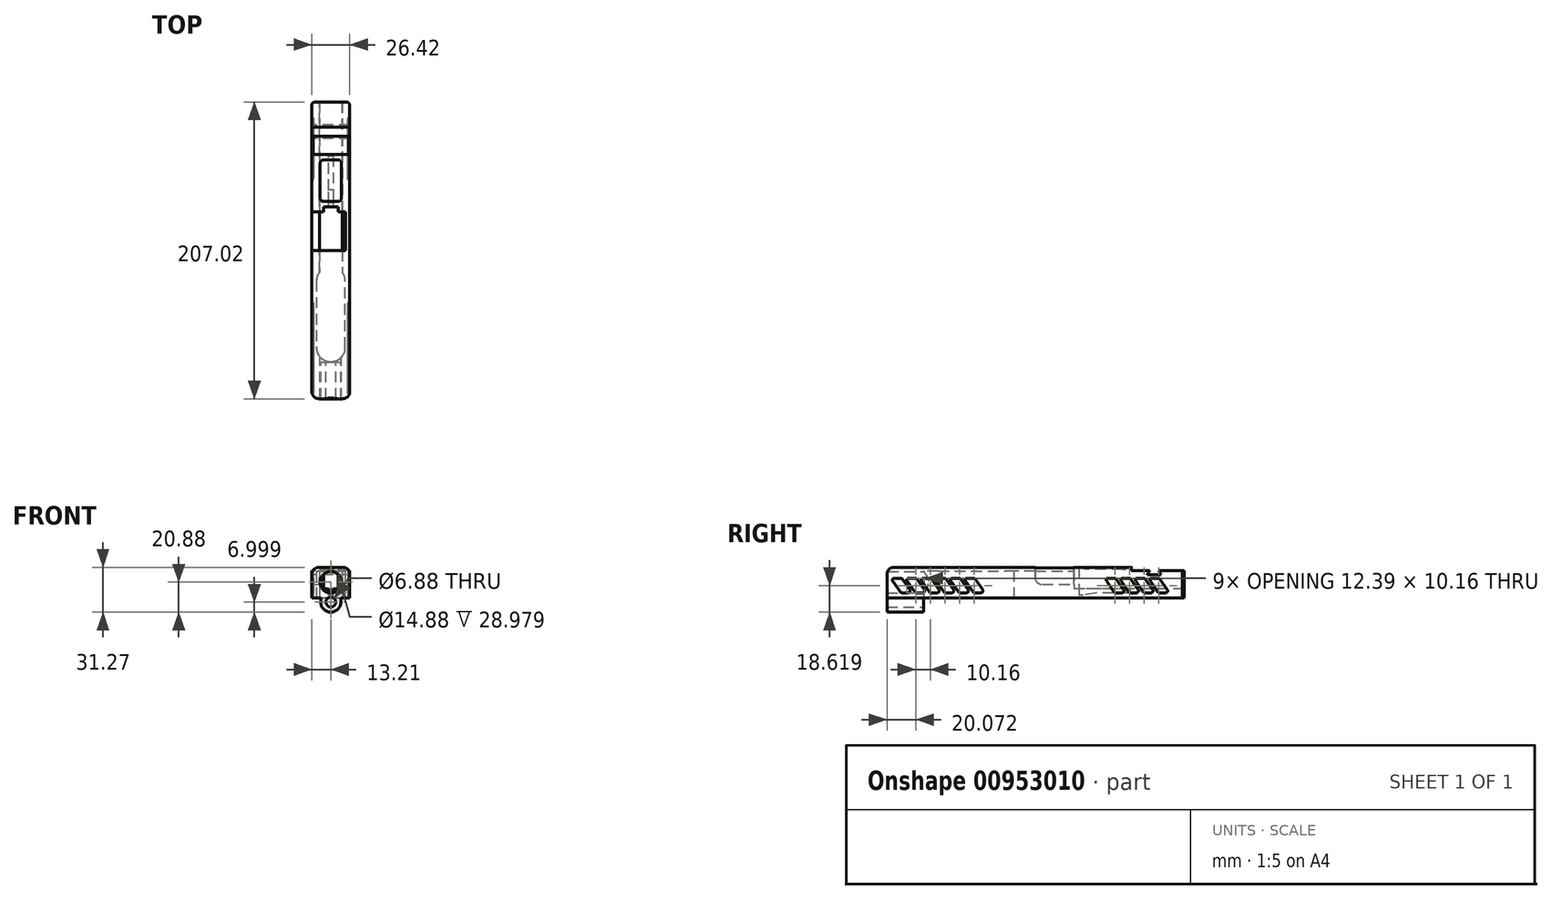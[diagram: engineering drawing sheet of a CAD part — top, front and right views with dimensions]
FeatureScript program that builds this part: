
annotation { "Feature Type Name" : "Feature", "Feature Type Description" : "" }
export const myFeature = defineFeature(function(context is Context, id is Id, definition is map)
    precondition{}
    {
        {
            var Q0;
            Q0=qCreatedBy(makeId("Front.planeOp"),FACE);
            var sketch = newSketch(context, id + "F0", { "sketchPlane" : qUnion([Q0])});
            skLineSegment(sketch, "E0.top", {"start": v(-13.2, 10.39) * mm, "end": v(13.2, 10.39) * mm});
            skLineSegment(sketch, "E0.left", {"start": v(-13.2, -11.1) * mm, "end": v(-13.2, 10.39) * mm});
            skLineSegment(sketch, "E0.right", {"start": v(13.2, -11.1) * mm, "end": v(13.2, 10.39) * mm});
            skLineSegment(sketch, "E1", {"start": v(-13.2, -11.1) * mm, "end": v(-7, -11.1) * mm});
            skLineSegment(sketch, "E2", {"start": v(-7, -11.1) * mm, "end": v(-7, -13.88) * mm});
            skLineSegment(sketch, "E3", {"start": v(13.2, -11.1) * mm, "end": v(7, -11.1) * mm});
            skLineSegment(sketch, "E4", {"start": v(7, -11.1) * mm, "end": v(7, -13.88) * mm});
            skArc(sketch, "E5", {"start": v(-7, -13.88) * mm, "mid": v(0, -20.88) * mm, "end": v(7, -13.88) * mm});
            skCircle(sketch, "E6", {"center": v(0, -13.88) * mm, "radius": 3.44 * mm});
            skCircle(sketch, "E7", {"center": v(0, 0) * mm, "radius": 7.44 * mm});
            skSolve(sketch);
        }
        {
            var Q0;
            Q0=makeQuery(id+"F0.imprint","IMPRINT",FACE,{"disambiguationData":[TD([[makeQuery(id+"F0.imprint","IMPRINT",EDGE,{"derivedFrom":sQuery(id+"F0.wireOp",EDGE,"E0.top")}),-1.0]])]});
            extrude(context, id + "F1", {"entities" : qUnion([Q0]), "endBound" : BoundingType.SYMMETRIC, "depth" : 207 * mm, "offsetDistance" : 25.4 * mm});
        }
        {
            var Q0;
            Q0=makeQuery(id+"F1.opExtrude","SWEPT_FACE",FACE,{"disambiguationData":[OSD([sQuery(id+"F0.wireOp",EDGE,"E0.left")])]});
            var sketch = newSketch(context, id + "F2", { "sketchPlane" : qUnion([Q0])});
            skLineSegment(sketch, "E8.bottom", {"start": v(-103.5, 10.39) * mm, "end": v(103.5, 10.39) * mm});
            skLineSegment(sketch, "E8.left", {"start": v(-103.5, 10.39) * mm, "end": v(-103.5, -11.1) * mm});
            skLineSegment(sketch, "E9", {"start": v(-103.5, -11.1) * mm, "end": v(77.85, -11.1) * mm});
            skLineSegment(sketch, "E10", {"start": v(77.85, -11.1) * mm, "end": v(77.85, -20.93) * mm});
            skLineSegment(sketch, "E11", {"start": v(77.85, -20.93) * mm, "end": v(103.5, -20.93) * mm});
            skLineSegment(sketch, "E12", {"start": v(103.5, -20.93) * mm, "end": v(103.5, 10.39) * mm});
            skSolve(sketch);
        }
        {
            var Q0;
            {var subQ2=sQuery(id+"F2.wireOp",EDGE,"E8.bottom");Q0=makeQuery(id+"F2.imprint","IMPRINT",FACE,{"disambiguationData":[TD([[makeQuery(id+"F2.imprint","IMPRINT",EDGE,{"derivedFrom":subQ2}),1.0]])]});}
            var Q1;
            {var subQ0=sQuery(id+"F2.wireOp",EDGE,"E10");Q1=makeQuery(id+"F2.imprint","IMPRINT",FACE,{"disambiguationData":[TD([[makeQuery(id+"F2.imprint","IMPRINT",EDGE,{"derivedFrom":subQ0}),1.0]])]});}
            extrude(context, id + "F3", {"entities" : qUnion([Q0, Q1]), "operationType" : NewBodyOperationType.INTERSECT, "endBound" : BoundingType.SYMMETRIC, "depth" : 115.82 * mm, "offsetDistance" : 25.4 * mm});
        }
        {
            var Q0;
            Q0=makeQuery(id+"F1.opExtrude","SWEPT_FACE",FACE,{"disambiguationData":[OSD([sQuery(id+"F0.wireOp",EDGE,"E0.top")])]});
            var sketch = newSketch(context, id + "F4", { "sketchPlane" : qUnion([Q0])});
            skLineSegment(sketch, "E13", {"start": v(-8.89, -103.5) * mm, "end": v(-8.89, -61.6) * mm});
            skLineSegment(sketch, "E14", {"start": v(-8.89, -103.5) * mm, "end": v(8.89, -103.5) * mm});
            skLineSegment(sketch, "E15", {"start": v(8.9, -103.5) * mm, "end": v(8.9, -61.6) * mm});
            skArc(sketch, "E16", {"start": v(8.9, -61.6) * mm, "mid": v(0, -52.7) * mm, "end": v(-8.89, -61.6) * mm});
            skLineSegment(sketch, "E17", {"start": v(-8.89, -61.6) * mm, "end": v(-8.9, -33.66) * mm});
            skLineSegment(sketch, "E18", {"start": v(-8.89, -33.66) * mm, "end": v(8.89, -33.66) * mm});
            skLineSegment(sketch, "E19", {"start": v(8.89, -33.66) * mm, "end": v(8.9, -61.6) * mm});
            skSolve(sketch);
        }
        {
            var Q0;
            Q0=makeQuery(id+"F1.opExtrude","SWEPT_FACE",FACE,{"disambiguationData":[OSD([sQuery(id+"F0.wireOp",EDGE,"E0.left")])]});
            var sketch = newSketch(context, id + "F5", { "sketchPlane" : qUnion([Q0])});
            skLineSegment(sketch, "E20", {"start": v(-93.35, -7.34) * mm, "end": v(-86.23, 2.82) * mm});
            skLineSegment(sketch, "E21", {"start": v(-86.23, 2.82) * mm, "end": v(-78.61, 2.82) * mm});
            skLineSegment(sketch, "E22", {"start": v(-78.61, 2.82) * mm, "end": v(-85.73, -7.34) * mm});
            skLineSegment(sketch, "E23", {"start": v(-85.73, -7.34) * mm, "end": v(-93.35, -7.34) * mm});
            skLineSegment(sketch, "E24", {"start": v(-83.19, -7.34) * mm, "end": v(-76.07, 2.82) * mm});
            skLineSegment(sketch, "E25", {"start": v(-76.07, 2.82) * mm, "end": v(-68.45, 2.82) * mm});
            skLineSegment(sketch, "E26", {"start": v(-68.45, 2.82) * mm, "end": v(-75.57, -7.34) * mm});
            skLineSegment(sketch, "E27", {"start": v(-75.57, -7.34) * mm, "end": v(-83.19, -7.34) * mm});
            skLineSegment(sketch, "E28", {"start": v(-73.03, -7.34) * mm, "end": v(-65.91, 2.82) * mm});
            skLineSegment(sketch, "E29", {"start": v(-65.91, 2.82) * mm, "end": v(-58.3, 2.82) * mm});
            skLineSegment(sketch, "E30", {"start": v(-58.3, 2.82) * mm, "end": v(-65.4, -7.34) * mm});
            skLineSegment(sketch, "E31", {"start": v(-65.4, -7.34) * mm, "end": v(-73.03, -7.34) * mm});
            skLineSegment(sketch, "E32", {"start": v(-62.87, -7.34) * mm, "end": v(-55.75, 2.82) * mm});
            skLineSegment(sketch, "E33", {"start": v(-55.75, 2.82) * mm, "end": v(-48.13, 2.82) * mm});
            skLineSegment(sketch, "E34", {"start": v(-48.13, 2.82) * mm, "end": v(-55.25, -7.34) * mm});
            skLineSegment(sketch, "E35", {"start": v(-55.25, -7.34) * mm, "end": v(-62.87, -7.34) * mm});
            skLineSegment(sketch, "E36", {"start": v(45.6, -7.34) * mm, "end": v(52.7, 2.82) * mm});
            skLineSegment(sketch, "E37", {"start": v(52.7, 2.82) * mm, "end": v(60.33, 2.82) * mm});
            skLineSegment(sketch, "E38", {"start": v(60.33, 2.82) * mm, "end": v(53.21, -7.34) * mm});
            skLineSegment(sketch, "E39", {"start": v(53.21, -7.34) * mm, "end": v(45.6, -7.34) * mm});
            skLineSegment(sketch, "E40", {"start": v(55.75, -7.34) * mm, "end": v(62.87, 2.82) * mm});
            skLineSegment(sketch, "E41", {"start": v(62.87, 2.82) * mm, "end": v(70.49, 2.82) * mm});
            skLineSegment(sketch, "E42", {"start": v(70.49, 2.82) * mm, "end": v(63.37, -7.34) * mm});
            skLineSegment(sketch, "E43", {"start": v(63.37, -7.34) * mm, "end": v(55.75, -7.34) * mm});
            skLineSegment(sketch, "E44", {"start": v(65.91, -7.34) * mm, "end": v(73.03, 2.82) * mm});
            skLineSegment(sketch, "E45", {"start": v(73.03, 2.82) * mm, "end": v(80.65, 2.82) * mm});
            skLineSegment(sketch, "E46", {"start": v(80.65, 2.82) * mm, "end": v(73.53, -7.34) * mm});
            skLineSegment(sketch, "E47", {"start": v(73.53, -7.34) * mm, "end": v(65.91, -7.34) * mm});
            skLineSegment(sketch, "E48", {"start": v(76.07, -7.34) * mm, "end": v(83.19, 2.82) * mm});
            skLineSegment(sketch, "E49", {"start": v(83.19, 2.82) * mm, "end": v(90.8, 2.82) * mm});
            skLineSegment(sketch, "E50", {"start": v(90.8, 2.82) * mm, "end": v(83.7, -7.34) * mm});
            skLineSegment(sketch, "E51", {"start": v(83.7, -7.34) * mm, "end": v(76.07, -7.34) * mm});
            skLineSegment(sketch, "E52", {"start": v(35.43, -7.34) * mm, "end": v(42.55, 2.82) * mm});
            skLineSegment(sketch, "E53", {"start": v(42.55, 2.82) * mm, "end": v(50.17, 2.82) * mm});
            skLineSegment(sketch, "E54", {"start": v(50.17, 2.82) * mm, "end": v(43.05, -7.34) * mm});
            skLineSegment(sketch, "E55", {"start": v(43.05, -7.34) * mm, "end": v(35.43, -7.34) * mm});
            skLineSegment(sketch, "E56", {"start": v(86.23, -7.34) * mm, "end": v(93.35, 2.82) * mm});
            skLineSegment(sketch, "E57", {"start": v(93.35, 2.82) * mm, "end": v(100.97, 2.82) * mm});
            skLineSegment(sketch, "E58", {"start": v(100.97, 2.82) * mm, "end": v(93.85, -7.34) * mm});
            skLineSegment(sketch, "E59", {"start": v(93.85, -7.34) * mm, "end": v(86.23, -7.34) * mm});
            skSolve(sketch);
        }
        {
            var Q0;
            Q0=makeQuery(id+"F3.boolean.opBoolean","MERGE",FACE,{"derivedFrom":[makeQuery(id+"F1.opExtrude","SWEPT_FACE",FACE,{"disambiguationData":[OSD([sQuery(id+"F0.wireOp",EDGE,"E3")])]})],"fromTools":[makeQuery(id+"F3.boolean.toolComplement.opBoolean","COPY",FACE,{"derivedFrom":makeQuery(id+"F3.opExtrude","SWEPT_FACE",FACE,{"disambiguationData":[OSD([sQuery(id+"F2.wireOp",EDGE,"E9")])]})})]});
            var sketch = newSketch(context, id + "F6", { "sketchPlane" : qUnion([Q0])});
            skLineSegment(sketch, "E60.left", {"start": v(-10, 21.26) * mm, "end": v(-10, 67.84) * mm});
            skLineSegment(sketch, "E61", {"start": v(-8, -26.72) * mm, "end": v(-5, -26.72) * mm});
            skLineSegment(sketch, "E62", {"start": v(-5, -26.72) * mm, "end": v(-5, -30.22) * mm});
            skLineSegment(sketch, "E63", {"start": v(-5, -30.22) * mm, "end": v(5, -30.22) * mm});
            skLineSegment(sketch, "E64", {"start": v(5, -30.22) * mm, "end": v(5, -26.72) * mm});
            skLineSegment(sketch, "E65", {"start": v(5, -26.72) * mm, "end": v(8, -26.72) * mm});
            skArc(sketch, "E66", {"start": v(-10, 21.26) * mm, "mid": v(-9.5, 18.1) * mm, "end": v(-8, 15.25) * mm});
            skArc(sketch, "E67", {"start": v(10, 67.84) * mm, "mid": v(0, 77.85) * mm, "end": v(-10, 67.84) * mm});
            skLineSegment(sketch, "E68", {"start": v(10, 67.84) * mm, "end": v(10, 21.26) * mm});
            skArc(sketch, "E69", {"start": v(8, 15.25) * mm, "mid": v(9.5, 18.1) * mm, "end": v(10, 21.26) * mm});
            skLineSegment(sketch, "E70", {"start": v(-8, 0.28) * mm, "end": v(-8, 15.25) * mm});
            skLineSegment(sketch, "E71", {"start": v(-8, 0.28) * mm, "end": v(8, 0.28) * mm});
            skLineSegment(sketch, "E72", {"start": v(-8, 0.28) * mm, "end": v(-8, -26.72) * mm});
            skLineSegment(sketch, "E73", {"start": v(8, -26.72) * mm, "end": v(8, 0.28) * mm});
            skLineSegment(sketch, "E74", {"start": v(8, 0.28) * mm, "end": v(8, 15.25) * mm});
            skLineSegment(sketch, "E75", {"start": v(8, -26.72) * mm, "end": v(8, -103.5) * mm});
            skLineSegment(sketch, "E76", {"start": v(8, -103.5) * mm, "end": v(-8, -103.5) * mm});
            skLineSegment(sketch, "E77", {"start": v(-8, -103.5) * mm, "end": v(-8, -26.72) * mm});
            skLineSegment(sketch, "E78", {"start": v(-1.5, -30.22) * mm, "end": v(-1.5, -65.73) * mm});
            skLineSegment(sketch, "E79", {"start": v(-1.5, -65.73) * mm, "end": v(1.5, -65.73) * mm});
            skLineSegment(sketch, "E80", {"start": v(1.5, -65.73) * mm, "end": v(1.5, -30.22) * mm});
            skLineSegment(sketch, "E81", {"start": v(-1.5, -33.22) * mm, "end": v(1.5, -33.22) * mm});
            skLineSegment(sketch, "E82", {"start": v(-1.5, -42.21) * mm, "end": v(1.5, -42.21) * mm});
            skSolve(sketch);
        }
        {
            var Q0;
            Q0=makeQuery(id+"F6.imprint","IMPRINT",FACE,{"disambiguationData":[TD([[makeQuery(id+"F6.imprint","IMPRINT",EDGE,{"derivedFrom":sQuery(id+"F6.wireOp",EDGE,"E61")}),1.0]])]});
            var Q1;
            {var subQ0=sQuery(id+"F6.wireOp",EDGE,"E64");Q1=makeQuery(id+"F6.imprint","IMPRINT",FACE,{"disambiguationData":[TD([[makeQuery(id+"F6.imprint","IMPRINT",EDGE,{"derivedFrom":subQ0}),1.0]])]});}
            extrude(context, id + "F7", {"entities" : qUnion([Q0, Q1]), "operationType" : NewBodyOperationType.REMOVE, "oppositeDirection" : true, "depth" : 25.4 * mm, "offsetDistance" : 25.4 * mm});
        }
        {
            var Q0;
            {var subQ1=sQuery(id+"F6.wireOp",EDGE,"E60.left");Q0=makeQuery(id+"F6.imprint","IMPRINT",FACE,{"disambiguationData":[TD([[makeQuery(id+"F6.imprint","IMPRINT",EDGE,{"derivedFrom":subQ1}),-1.0]])]});}
            var Q1;
            {var subQ6=sQuery(id+"F6.wireOp",EDGE,"E68");Q1=makeQuery(id+"F6.imprint","IMPRINT",FACE,{"disambiguationData":[TD([[makeQuery(id+"F6.imprint","IMPRINT",EDGE,{"derivedFrom":subQ6}),-1.0]])]});}
            extrude(context, id + "F8", {"entities" : qUnion([Q0, Q1]), "operationType" : NewBodyOperationType.REMOVE, "oppositeDirection" : true, "depth" : 19 * mm, "offsetDistance" : 25.4 * mm});
        }
        {
            var Q0;
            Q0=makeQuery(id+"F8.boolean.opBoolean","MERGE",FACE,{"derivedFrom":[makeQuery(id+"F7.boolean.opBoolean","COPY",FACE,{"derivedFrom":makeQuery(id+"F7.opExtrude","SWEPT_FACE",FACE,{"disambiguationData":[OSD([sQuery(id+"F6.wireOp",EDGE,"E72")])]})})],"fromTools":[makeQuery(id+"F8.opExtrude","SWEPT_FACE",FACE,{"disambiguationData":[OSD([sQuery(id+"F6.wireOp",EDGE,"E70")])]})]});
            var sketch = newSketch(context, id + "F9", { "sketchPlane" : qUnion([Q0])});
            skLineSegment(sketch, "E83.bottom", {"start": v(-0.28, 10.39) * mm, "end": v(26.72, 10.39) * mm});
            skLineSegment(sketch, "E83.top", {"start": v(-0.28, -1.6) * mm, "end": v(26.72, -1.6) * mm});
            skLineSegment(sketch, "E83.left", {"start": v(-0.28, 10.39) * mm, "end": v(-0.28, -1.6) * mm});
            skLineSegment(sketch, "E83.right", {"start": v(26.72, 10.39) * mm, "end": v(26.72, -1.6) * mm});
            skSolve(sketch);
        }
        {
            var Q0;
            Q0=makeQuery(id+"F7.boolean.opBoolean","INTERSECT",EDGE,{"derivedFrom":[makeQuery(id+"F1.opExtrude","SWEPT_FACE",FACE,{"disambiguationData":[OSD([sQuery(id+"F0.wireOp",EDGE,"E0.top")])]}),makeQuery(id+"F7.opExtrude","SWEPT_FACE",FACE,{"disambiguationData":[OSD([sQuery(id+"F6.wireOp",EDGE,"E73")])]})]});
            chamfer(context, id + "F10", {"entities" : qUnion([Q0]), "width" : 2.5 * mm, "tangentPropagation" : true});
        }
        {
            var Q0;
            {var subQ5=sQuery(id+"F6.wireOp",EDGE,"E81");Q0=makeQuery(id+"F6.imprint","IMPRINT",FACE,{"disambiguationData":[TD([[makeQuery(id+"F6.imprint","IMPRINT",EDGE,{"derivedFrom":subQ5}),1.0]])]});}
            var Q1;
            {var subQ0=sQuery(id+"F6.wireOp",EDGE,"E81");Q1=makeQuery(id+"F6.imprint","IMPRINT",FACE,{"disambiguationData":[TD([[makeQuery(id+"F6.imprint","IMPRINT",EDGE,{"derivedFrom":subQ0}),-1.0]])]});}
            var Q2;
            {var subQ0=sQuery(id+"F6.wireOp",EDGE,"E79");Q2=makeQuery(id+"F6.imprint","IMPRINT",FACE,{"disambiguationData":[TD([[makeQuery(id+"F6.imprint","IMPRINT",EDGE,{"derivedFrom":subQ0}),1.0]])]});}
            var Q3;
            Q3=makeQuery(id+"F6.imprint","IMPRINT",FACE,{"disambiguationData":[TD([[makeQuery(id+"F6.imprint","IMPRINT",EDGE,{"derivedFrom":sQuery(id+"F6.wireOp",EDGE,"E61")}),-1.0]])]});
            var Q4;
            {var subQ1=sQuery(id+"F6.wireOp",EDGE,"E64");Q4=makeQuery(id+"F6.imprint","IMPRINT",FACE,{"disambiguationData":[TD([[makeQuery(id+"F6.imprint","IMPRINT",EDGE,{"derivedFrom":subQ1}),-1.0]])]});}
            var Q5;
            Q5=makeQuery(id+"F10.opChamfer","SPLIT",FACE,{"disambiguationData":[OD(1.0)],"derivedFrom":makeQuery(id+"F1.opExtrude","SWEPT_FACE",FACE,{"disambiguationData":[OSD([sQuery(id+"F0.wireOp",EDGE,"E0.top")])]})});
            extrude(context, id + "F11", {"entities" : qUnion([Q0, Q1, Q2, Q3, Q4]), "operationType" : NewBodyOperationType.ADD, "endBound" : BoundingType.UP_TO_SURFACE, "oppositeDirection" : true, "depth" : 25.4 * mm, "endBoundEntityFace" : qUnion([Q5]), "offsetDistance" : 25.4 * mm});
        }
        {
            var Q0;
            Q0=makeQuery(id+"F6.imprint","IMPRINT",FACE,{"disambiguationData":[TD([[makeQuery(id+"F6.imprint","IMPRINT",EDGE,{"derivedFrom":sQuery(id+"F6.wireOp",EDGE,"E61")}),-1.0]])]});
            var Q1;
            {var subQ1=sQuery(id+"F6.wireOp",EDGE,"E64");Q1=makeQuery(id+"F6.imprint","IMPRINT",FACE,{"disambiguationData":[TD([[makeQuery(id+"F6.imprint","IMPRINT",EDGE,{"derivedFrom":subQ1}),-1.0]])]});}
            extrude(context, id + "F12", {"entities" : qUnion([Q0, Q1]), "operationType" : NewBodyOperationType.REMOVE, "oppositeDirection" : true, "depth" : 6.48 * mm, "offsetDistance" : 25.4 * mm});
        }
        {
            var Q0;
            {var subQ5=sQuery(id+"F6.wireOp",EDGE,"E81");Q0=makeQuery(id+"F6.imprint","IMPRINT",FACE,{"disambiguationData":[TD([[makeQuery(id+"F6.imprint","IMPRINT",EDGE,{"derivedFrom":subQ5}),1.0]])]});}
            extrude(context, id + "F13", {"entities" : qUnion([Q0]), "operationType" : NewBodyOperationType.ADD, "oppositeDirection" : true, "depth" : 1.98 * mm, "offsetDistance" : 25.4 * mm});
        }
        {
            var Q0;
            Q0=makeQuery(id+"F12.boolean.opBoolean","COPY",FACE,{"derivedFrom":makeQuery(id+"F12.opExtrude","SWEPT_FACE",FACE,{"disambiguationData":[OSD([sQuery(id+"F6.wireOp",EDGE,"E78")])]})});
            var sketch = newSketch(context, id + "F14", { "sketchPlane" : qUnion([Q0])});
            skLineSegment(sketch, "E84", {"start": v(-30.22, -11.1) * mm, "end": v(-30.22, -9.12) * mm});
            skLineSegment(sketch, "E85", {"start": v(-30.22, -9.12) * mm, "end": v(-33.22, -9.12) * mm});
            skLineSegment(sketch, "E86", {"start": v(-33.22, -9.12) * mm, "end": v(-42.21, -7.62) * mm});
            skLineSegment(sketch, "E87", {"start": v(-42.21, -7.62) * mm, "end": v(-65.73, -7.62) * mm});
            skPoint(sketch, "E87.endSnap0", {"position": v(-65.73, -7.86) * mm});
            skLineSegment(sketch, "E88", {"start": v(-65.73, -7.62) * mm, "end": v(-65.73, -11.1) * mm});
            skLineSegment(sketch, "E89", {"start": v(-65.73, -11.1) * mm, "end": v(-30.22, -11.1) * mm});
            skSolve(sketch);
        }
        {
            var Q0;
            Q0=makeQuery(id+"F14.imprint","IMPRINT",FACE,{"disambiguationData":[TD([[makeQuery(id+"F14.imprint","IMPRINT",EDGE,{"derivedFrom":sQuery(id+"F14.wireOp",EDGE,"E84")}),-1.0]])]});
            extrude(context, id + "F15", {"entities" : qUnion([Q0]), "operationType" : NewBodyOperationType.REMOVE, "oppositeDirection" : true, "depth" : 4.06 * mm, "offsetDistance" : 25.4 * mm});
        }
        {
            var Q0;
            Q0=makeQuery(id+"F1.opExtrude","SWEPT_FACE",FACE,{"disambiguationData":[OSD([sQuery(id+"F0.wireOp",EDGE,"E0.left")])]});
            var sketch = newSketch(context, id + "F16", { "sketchPlane" : qUnion([Q0])});
            skLineSegment(sketch, "E90", {"start": v(-103.5, 11.76) * mm, "end": v(-66.93, 11.76) * mm});
            skLineSegment(sketch, "E91", {"start": v(-66.93, 11.76) * mm, "end": v(-66.93, 7.95) * mm});
            skLineSegment(sketch, "E92", {"start": v(-66.93, 7.95) * mm, "end": v(-79.44, 7.95) * mm});
            skLineSegment(sketch, "E93", {"start": v(-79.44, 7.95) * mm, "end": v(-77.9, 5.28) * mm});
            skLineSegment(sketch, "E94", {"start": v(-77.9, 5.28) * mm, "end": v(-87.43, 5.28) * mm});
            skLineSegment(sketch, "E95", {"start": v(-87.43, 5.28) * mm, "end": v(-85.89, 7.95) * mm});
            skLineSegment(sketch, "E96", {"start": v(-85.89, 7.95) * mm, "end": v(-103.5, 7.95) * mm});
            skLineSegment(sketch, "E97", {"start": v(-103.5, 11.76) * mm, "end": v(-103.5, 7.95) * mm});
            skSolve(sketch);
        }
        {
            var Q0;
            {var subQ9=sQuery(id+"F16.wireOp",EDGE,"E90");Q0=makeQuery(id+"F16.imprint","IMPRINT",FACE,{"disambiguationData":[TD([[makeQuery(id+"F16.imprint","IMPRINT",EDGE,{"derivedFrom":subQ9}),-1.0]])]});}
            var Q1;
            {var subQ8=sQuery(id+"F16.wireOp",EDGE,"IXoennea-lvBA-JRsV-betp-ysQFHRv7K1wK");Q1=makeQuery(id+"F16.imprint","IMPRINT",FACE,{"disambiguationData":[TD([[makeQuery(id+"F16.imprint","IMPRINT",EDGE,{"derivedFrom":subQ8}),1.0]])]});}
            var Q2;
            {var subQ0=sQuery(id+"F16.wireOp",EDGE,"E93");Q2=makeQuery(id+"F16.imprint","IMPRINT",FACE,{"disambiguationData":[TD([[makeQuery(id+"F16.imprint","IMPRINT",EDGE,{"derivedFrom":subQ0}),-1.0]])]});}
            extrude(context, id + "F17", {"entities" : qUnion([Q0, Q1, Q2]), "operationType" : NewBodyOperationType.REMOVE, "oppositeDirection" : true, "depth" : 44.2 * mm, "offsetDistance" : 25.4 * mm});
        }
        {
            var Q0;
            Q0=makeQuery(id+"F5.imprint","IMPRINT",FACE,{"disambiguationData":[TD([[makeQuery(id+"F5.imprint","IMPRINT",EDGE,{"derivedFrom":sQuery(id+"F5.wireOp",EDGE,"E20")}),-1.0]])]});
            var Q1;
            Q1=makeQuery(id+"F5.imprint","IMPRINT",FACE,{"disambiguationData":[TD([[makeQuery(id+"F5.imprint","IMPRINT",EDGE,{"derivedFrom":sQuery(id+"F5.wireOp",EDGE,"E24")}),-1.0]])]});
            var Q2;
            Q2=makeQuery(id+"F5.imprint","IMPRINT",FACE,{"disambiguationData":[TD([[makeQuery(id+"F5.imprint","IMPRINT",EDGE,{"derivedFrom":sQuery(id+"F5.wireOp",EDGE,"E28")}),-1.0]])]});
            var Q3;
            Q3=makeQuery(id+"F5.imprint","IMPRINT",FACE,{"disambiguationData":[TD([[makeQuery(id+"F5.imprint","IMPRINT",EDGE,{"derivedFrom":sQuery(id+"F5.wireOp",EDGE,"E32")}),-1.0]])]});
            var Q4;
            Q4=qSketchRegion(id+"F9",true);
            var Q5;
            Q5=makeQuery(id+"F5.imprint","IMPRINT",FACE,{"disambiguationData":[TD([[makeQuery(id+"F5.imprint","IMPRINT",EDGE,{"derivedFrom":sQuery(id+"F5.wireOp",EDGE,"E36")}),-1.0]])]});
            var Q6;
            Q6=makeQuery(id+"F5.imprint","IMPRINT",FACE,{"disambiguationData":[TD([[makeQuery(id+"F5.imprint","IMPRINT",EDGE,{"derivedFrom":sQuery(id+"F5.wireOp",EDGE,"E40")}),-1.0]])]});
            var Q7;
            Q7=makeQuery(id+"F5.imprint","IMPRINT",FACE,{"disambiguationData":[TD([[makeQuery(id+"F5.imprint","IMPRINT",EDGE,{"derivedFrom":sQuery(id+"F5.wireOp",EDGE,"E44")}),-1.0]])]});
            var Q8;
            Q8=makeQuery(id+"F5.imprint","IMPRINT",FACE,{"disambiguationData":[TD([[makeQuery(id+"F5.imprint","IMPRINT",EDGE,{"derivedFrom":sQuery(id+"F5.wireOp",EDGE,"E48")}),-1.0]])]});
            var Q9;
            Q9=makeQuery(id+"F5.imprint","IMPRINT",FACE,{"disambiguationData":[TD([[makeQuery(id+"F5.imprint","IMPRINT",EDGE,{"derivedFrom":sQuery(id+"F5.wireOp",EDGE,"E52")}),-1.0]])]});
            var Q10;
            Q10=makeQuery(id+"F5.imprint","IMPRINT",FACE,{"disambiguationData":[TD([[makeQuery(id+"F5.imprint","IMPRINT",EDGE,{"derivedFrom":sQuery(id+"F5.wireOp",EDGE,"E56")}),-1.0]])]});
            extrude(context, id + "F18", {"entities" : qUnion([Q0, Q1, Q2, Q3, Q4, Q5, Q6, Q7, Q8, Q9, Q10]), "operationType" : NewBodyOperationType.REMOVE, "oppositeDirection" : true, "depth" : 1.27 * mm, "offsetDistance" : 25.4 * mm});
        }
        {
            var Q0;
            Q0=makeQuery(id+"F18.boolean.opBoolean","COPY",EDGE,{"derivedFrom":makeQuery(id+"F18.opExtrude","SWEPT_EDGE",EDGE,{"disambiguationData":[OSD([sQuery(id+"F5.wireOp",EDGE,"E20"),sQuery(id+"F5.wireOp",EDGE,"E21")])]})});
            var Q1;
            Q1=makeQuery(id+"F18.boolean.opBoolean","COPY",EDGE,{"derivedFrom":makeQuery(id+"F18.opExtrude","SWEPT_EDGE",EDGE,{"disambiguationData":[OSD([sQuery(id+"F5.wireOp",EDGE,"E24"),sQuery(id+"F5.wireOp",EDGE,"E25")])]})});
            var Q2;
            Q2=makeQuery(id+"F18.boolean.opBoolean","COPY",EDGE,{"derivedFrom":makeQuery(id+"F18.opExtrude","SWEPT_EDGE",EDGE,{"disambiguationData":[OSD([sQuery(id+"F5.wireOp",EDGE,"E28"),sQuery(id+"F5.wireOp",EDGE,"E29")])]})});
            var Q3;
            Q3=makeQuery(id+"F18.boolean.opBoolean","COPY",EDGE,{"derivedFrom":makeQuery(id+"F18.opExtrude","SWEPT_EDGE",EDGE,{"disambiguationData":[OSD([sQuery(id+"F5.wireOp",EDGE,"E32"),sQuery(id+"F5.wireOp",EDGE,"E33")])]})});
            var Q4;
            Q4=makeQuery(id+"F18.boolean.opBoolean","COPY",EDGE,{"derivedFrom":makeQuery(id+"F18.opExtrude","SWEPT_EDGE",EDGE,{"disambiguationData":[OSD([sQuery(id+"F5.wireOp",EDGE,"E21"),sQuery(id+"F5.wireOp",EDGE,"E22")])]})});
            var Q5;
            Q5=makeQuery(id+"F18.boolean.opBoolean","COPY",EDGE,{"derivedFrom":makeQuery(id+"F18.opExtrude","SWEPT_EDGE",EDGE,{"disambiguationData":[OSD([sQuery(id+"F5.wireOp",EDGE,"E25"),sQuery(id+"F5.wireOp",EDGE,"E26")])]})});
            var Q6;
            Q6=makeQuery(id+"F18.boolean.opBoolean","COPY",EDGE,{"derivedFrom":makeQuery(id+"F18.opExtrude","SWEPT_EDGE",EDGE,{"disambiguationData":[OSD([sQuery(id+"F5.wireOp",EDGE,"E29"),sQuery(id+"F5.wireOp",EDGE,"E30")])]})});
            var Q7;
            Q7=makeQuery(id+"F18.boolean.opBoolean","COPY",EDGE,{"derivedFrom":makeQuery(id+"F18.opExtrude","SWEPT_EDGE",EDGE,{"disambiguationData":[OSD([sQuery(id+"F5.wireOp",EDGE,"E33"),sQuery(id+"F5.wireOp",EDGE,"E34")])]})});
            var Q8;
            Q8=makeQuery(id+"F18.boolean.opBoolean","COPY",EDGE,{"derivedFrom":makeQuery(id+"F18.opExtrude","SWEPT_EDGE",EDGE,{"disambiguationData":[OSD([sQuery(id+"F5.wireOp",EDGE,"E34"),sQuery(id+"F5.wireOp",EDGE,"E35")])]})});
            var Q9;
            Q9=makeQuery(id+"F18.boolean.opBoolean","COPY",EDGE,{"derivedFrom":makeQuery(id+"F18.opExtrude","SWEPT_EDGE",EDGE,{"disambiguationData":[OSD([sQuery(id+"F5.wireOp",EDGE,"E30"),sQuery(id+"F5.wireOp",EDGE,"E31")])]})});
            var Q10;
            Q10=makeQuery(id+"F18.boolean.opBoolean","COPY",EDGE,{"derivedFrom":makeQuery(id+"F18.opExtrude","SWEPT_EDGE",EDGE,{"disambiguationData":[OSD([sQuery(id+"F5.wireOp",EDGE,"E26"),sQuery(id+"F5.wireOp",EDGE,"E27")])]})});
            var Q11;
            Q11=makeQuery(id+"F18.boolean.opBoolean","COPY",EDGE,{"derivedFrom":makeQuery(id+"F18.opExtrude","SWEPT_EDGE",EDGE,{"disambiguationData":[OSD([sQuery(id+"F5.wireOp",EDGE,"E22"),sQuery(id+"F5.wireOp",EDGE,"E23")])]})});
            var Q12;
            Q12=makeQuery(id+"F18.boolean.opBoolean","COPY",EDGE,{"derivedFrom":makeQuery(id+"F18.opExtrude","SWEPT_EDGE",EDGE,{"disambiguationData":[OSD([sQuery(id+"F5.wireOp",EDGE,"E20"),sQuery(id+"F5.wireOp",EDGE,"E23")])]})});
            var Q13;
            Q13=makeQuery(id+"F18.boolean.opBoolean","COPY",EDGE,{"derivedFrom":makeQuery(id+"F18.opExtrude","SWEPT_EDGE",EDGE,{"disambiguationData":[OSD([sQuery(id+"F5.wireOp",EDGE,"E24"),sQuery(id+"F5.wireOp",EDGE,"E27")])]})});
            var Q14;
            Q14=makeQuery(id+"F18.boolean.opBoolean","COPY",EDGE,{"derivedFrom":makeQuery(id+"F18.opExtrude","SWEPT_EDGE",EDGE,{"disambiguationData":[OSD([sQuery(id+"F5.wireOp",EDGE,"E28"),sQuery(id+"F5.wireOp",EDGE,"E31")])]})});
            var Q15;
            Q15=makeQuery(id+"F18.boolean.opBoolean","COPY",EDGE,{"derivedFrom":makeQuery(id+"F18.opExtrude","SWEPT_EDGE",EDGE,{"disambiguationData":[OSD([sQuery(id+"F5.wireOp",EDGE,"E32"),sQuery(id+"F5.wireOp",EDGE,"E35")])]})});
            var Q16;
            Q16=makeQuery(id+"F18.boolean.opBoolean","COPY",EDGE,{"derivedFrom":makeQuery(id+"F18.opExtrude","SWEPT_EDGE",EDGE,{"disambiguationData":[OSD([sQuery(id+"F5.wireOp",EDGE,"E37"),sQuery(id+"F5.wireOp",EDGE,"E38")])]})});
            var Q17;
            Q17=makeQuery(id+"F18.boolean.opBoolean","COPY",EDGE,{"derivedFrom":makeQuery(id+"F18.opExtrude","SWEPT_EDGE",EDGE,{"disambiguationData":[OSD([sQuery(id+"F5.wireOp",EDGE,"E41"),sQuery(id+"F5.wireOp",EDGE,"E42")])]})});
            var Q18;
            Q18=makeQuery(id+"F18.boolean.opBoolean","COPY",EDGE,{"derivedFrom":makeQuery(id+"F18.opExtrude","SWEPT_EDGE",EDGE,{"disambiguationData":[OSD([sQuery(id+"F5.wireOp",EDGE,"E45"),sQuery(id+"F5.wireOp",EDGE,"E46")])]})});
            var Q19;
            Q19=makeQuery(id+"F18.boolean.opBoolean","COPY",EDGE,{"derivedFrom":makeQuery(id+"F18.opExtrude","SWEPT_EDGE",EDGE,{"disambiguationData":[OSD([sQuery(id+"F5.wireOp",EDGE,"E49"),sQuery(id+"F5.wireOp",EDGE,"E50")])]})});
            var Q20;
            Q20=makeQuery(id+"F18.boolean.opBoolean","COPY",EDGE,{"derivedFrom":makeQuery(id+"F18.opExtrude","SWEPT_EDGE",EDGE,{"disambiguationData":[OSD([sQuery(id+"F5.wireOp",EDGE,"E50"),sQuery(id+"F5.wireOp",EDGE,"E51")])]})});
            var Q21;
            Q21=makeQuery(id+"F18.boolean.opBoolean","COPY",EDGE,{"derivedFrom":makeQuery(id+"F18.opExtrude","SWEPT_EDGE",EDGE,{"disambiguationData":[OSD([sQuery(id+"F5.wireOp",EDGE,"E46"),sQuery(id+"F5.wireOp",EDGE,"E47")])]})});
            var Q22;
            Q22=makeQuery(id+"F18.boolean.opBoolean","COPY",EDGE,{"derivedFrom":makeQuery(id+"F18.opExtrude","SWEPT_EDGE",EDGE,{"disambiguationData":[OSD([sQuery(id+"F5.wireOp",EDGE,"E42"),sQuery(id+"F5.wireOp",EDGE,"E43")])]})});
            var Q23;
            Q23=makeQuery(id+"F18.boolean.opBoolean","COPY",EDGE,{"derivedFrom":makeQuery(id+"F18.opExtrude","SWEPT_EDGE",EDGE,{"disambiguationData":[OSD([sQuery(id+"F5.wireOp",EDGE,"E38"),sQuery(id+"F5.wireOp",EDGE,"E39")])]})});
            var Q24;
            Q24=makeQuery(id+"F18.boolean.opBoolean","COPY",EDGE,{"derivedFrom":makeQuery(id+"F18.opExtrude","SWEPT_EDGE",EDGE,{"disambiguationData":[OSD([sQuery(id+"F5.wireOp",EDGE,"E48"),sQuery(id+"F5.wireOp",EDGE,"E51")])]})});
            var Q25;
            Q25=makeQuery(id+"F18.boolean.opBoolean","COPY",EDGE,{"derivedFrom":makeQuery(id+"F18.opExtrude","SWEPT_EDGE",EDGE,{"disambiguationData":[OSD([sQuery(id+"F5.wireOp",EDGE,"E40"),sQuery(id+"F5.wireOp",EDGE,"E43")])]})});
            var Q26;
            Q26=makeQuery(id+"F18.boolean.opBoolean","COPY",EDGE,{"derivedFrom":makeQuery(id+"F18.opExtrude","SWEPT_EDGE",EDGE,{"disambiguationData":[OSD([sQuery(id+"F5.wireOp",EDGE,"E36"),sQuery(id+"F5.wireOp",EDGE,"E39")])]})});
            var Q27;
            Q27=makeQuery(id+"F18.boolean.opBoolean","COPY",EDGE,{"derivedFrom":makeQuery(id+"F18.opExtrude","SWEPT_EDGE",EDGE,{"disambiguationData":[OSD([sQuery(id+"F5.wireOp",EDGE,"E44"),sQuery(id+"F5.wireOp",EDGE,"E47")])]})});
            var Q28;
            Q28=makeQuery(id+"F18.boolean.opBoolean","COPY",EDGE,{"derivedFrom":makeQuery(id+"F18.opExtrude","SWEPT_EDGE",EDGE,{"disambiguationData":[OSD([sQuery(id+"F5.wireOp",EDGE,"E48"),sQuery(id+"F5.wireOp",EDGE,"E49")])]})});
            var Q29;
            Q29=makeQuery(id+"F18.boolean.opBoolean","COPY",EDGE,{"derivedFrom":makeQuery(id+"F18.opExtrude","SWEPT_EDGE",EDGE,{"disambiguationData":[OSD([sQuery(id+"F5.wireOp",EDGE,"E44"),sQuery(id+"F5.wireOp",EDGE,"E45")])]})});
            var Q30;
            Q30=makeQuery(id+"F18.boolean.opBoolean","COPY",EDGE,{"derivedFrom":makeQuery(id+"F18.opExtrude","SWEPT_EDGE",EDGE,{"disambiguationData":[OSD([sQuery(id+"F5.wireOp",EDGE,"E40"),sQuery(id+"F5.wireOp",EDGE,"E41")])]})});
            var Q31;
            Q31=makeQuery(id+"F18.boolean.opBoolean","COPY",EDGE,{"derivedFrom":makeQuery(id+"F18.opExtrude","SWEPT_EDGE",EDGE,{"disambiguationData":[OSD([sQuery(id+"F5.wireOp",EDGE,"E36"),sQuery(id+"F5.wireOp",EDGE,"E37")])]})});
            var Q32;
            Q32=makeQuery(id+"F18.boolean.opBoolean","COPY",EDGE,{"derivedFrom":makeQuery(id+"F18.opExtrude","SWEPT_EDGE",EDGE,{"disambiguationData":[OSD([sQuery(id+"F5.wireOp",EDGE,"E52"),sQuery(id+"F5.wireOp",EDGE,"E53")])]})});
            var Q33;
            Q33=makeQuery(id+"F18.boolean.opBoolean","COPY",EDGE,{"derivedFrom":makeQuery(id+"F18.opExtrude","SWEPT_EDGE",EDGE,{"disambiguationData":[OSD([sQuery(id+"F5.wireOp",EDGE,"E57"),sQuery(id+"F5.wireOp",EDGE,"E58")])]})});
            var Q34;
            Q34=makeQuery(id+"F18.boolean.opBoolean","COPY",EDGE,{"derivedFrom":makeQuery(id+"F18.opExtrude","SWEPT_EDGE",EDGE,{"disambiguationData":[OSD([sQuery(id+"F5.wireOp",EDGE,"E53"),sQuery(id+"F5.wireOp",EDGE,"E54")])]})});
            var Q35;
            Q35=makeQuery(id+"F18.boolean.opBoolean","COPY",EDGE,{"derivedFrom":makeQuery(id+"F18.opExtrude","SWEPT_EDGE",EDGE,{"disambiguationData":[OSD([sQuery(id+"F5.wireOp",EDGE,"E56"),sQuery(id+"F5.wireOp",EDGE,"E57")])]})});
            var Q36;
            Q36=makeQuery(id+"F18.boolean.opBoolean","COPY",EDGE,{"derivedFrom":makeQuery(id+"F18.opExtrude","SWEPT_EDGE",EDGE,{"disambiguationData":[OSD([sQuery(id+"F5.wireOp",EDGE,"E56"),sQuery(id+"F5.wireOp",EDGE,"E59")])]})});
            var Q37;
            Q37=makeQuery(id+"F18.boolean.opBoolean","COPY",EDGE,{"derivedFrom":makeQuery(id+"F18.opExtrude","SWEPT_EDGE",EDGE,{"disambiguationData":[OSD([sQuery(id+"F5.wireOp",EDGE,"E52"),sQuery(id+"F5.wireOp",EDGE,"E55")])]})});
            var Q38;
            Q38=makeQuery(id+"F18.boolean.opBoolean","COPY",EDGE,{"derivedFrom":makeQuery(id+"F18.opExtrude","SWEPT_EDGE",EDGE,{"disambiguationData":[OSD([sQuery(id+"F5.wireOp",EDGE,"E54"),sQuery(id+"F5.wireOp",EDGE,"E55")])]})});
            var Q39;
            Q39=makeQuery(id+"F18.boolean.opBoolean","COPY",EDGE,{"derivedFrom":makeQuery(id+"F18.opExtrude","SWEPT_EDGE",EDGE,{"disambiguationData":[OSD([sQuery(id+"F5.wireOp",EDGE,"E58"),sQuery(id+"F5.wireOp",EDGE,"E59")])]})});
            fillet(context, id + "F19", {"entities" : qUnion([Q0, Q1, Q2, Q3, Q4, Q5, Q6, Q7, Q8, Q9, Q10, Q11, Q12, Q13, Q14, Q15, Q16, Q17, Q18, Q19, Q20, Q21, Q22, Q23, Q24, Q25, Q26, Q27, Q28, Q29, Q30, Q31, Q32, Q33, Q34, Q35, Q36, Q37, Q38, Q39]), "radius" : 1.27 * mm, "tangentPropagation" : true, "allowEdgeOverflow" : false});
        }
        {
            var Q0;
            Q0=makeQuery(id+"F10.opChamfer","SPLIT",FACE,{"disambiguationData":[OD(1.0)],"derivedFrom":makeQuery(id+"F1.opExtrude","SWEPT_FACE",FACE,{"disambiguationData":[OSD([sQuery(id+"F0.wireOp",EDGE,"E0.top")])]})});
            var sketch = newSketch(context, id + "F20", { "sketchPlane" : qUnion([Q0])});
            skLineSegment(sketch, "E98.bottom", {"start": v(-7.44, 63.12) * mm, "end": v(7.44, 63.12) * mm});
            skLineSegment(sketch, "E98.top", {"start": v(-7.44, 34.03) * mm, "end": v(7.44, 34.03) * mm});
            skLineSegment(sketch, "E98.left", {"start": v(-7.44, 63.12) * mm, "end": v(-7.44, 34.03) * mm});
            skLineSegment(sketch, "E98.right", {"start": v(7.44, 63.12) * mm, "end": v(7.44, 34.03) * mm});
            skSolve(sketch);
        }
        {
            var Q0;
            Q0=makeQuery(id+"F20.imprint","IMPRINT",FACE,{"disambiguationData":[TD([[makeQuery(id+"F20.imprint","IMPRINT",EDGE,{"derivedFrom":sQuery(id+"F20.wireOp",EDGE,"E98.bottom")}),-1.0]])]});
            extrude(context, id + "F21", {"entities" : qUnion([Q0]), "operationType" : NewBodyOperationType.REMOVE, "oppositeDirection" : true, "depth" : 1.27 * mm, "offsetDistance" : 25.4 * mm});
        }
        {
            var Q0;
            Q0=makeQuery(id+"F21.boolean.opBoolean","COPY",EDGE,{"derivedFrom":makeQuery(id+"F21.opExtrude","SWEPT_EDGE",EDGE,{"disambiguationData":[OSD([sQuery(id+"F20.wireOp",EDGE,"E98.bottom"),sQuery(id+"F20.wireOp",EDGE,"E98.left")])]})});
            var Q1;
            Q1=makeQuery(id+"FShAaVJqdzQdxkJ_1.boolean.opBoolean","COPY",EDGE,{"derivedFrom":makeQuery(id+"FShAaVJqdzQdxkJ_1.opExtrude","SWEPT_EDGE",EDGE,{"disambiguationData":[OSD([sQuery(id+"F4.wireOp",EDGE,"E17"),sQuery(id+"F4.wireOp",EDGE,"E18")])]})});
            var Q2;
            Q2=makeQuery(id+"FShAaVJqdzQdxkJ_1.boolean.opBoolean","COPY",EDGE,{"derivedFrom":makeQuery(id+"FShAaVJqdzQdxkJ_1.opExtrude","SWEPT_EDGE",EDGE,{"disambiguationData":[OSD([sQuery(id+"F4.wireOp",EDGE,"E18"),sQuery(id+"F4.wireOp",EDGE,"E19")])]})});
            var Q3;
            Q3=makeQuery(id+"F21.boolean.opBoolean","COPY",EDGE,{"derivedFrom":makeQuery(id+"F21.opExtrude","SWEPT_EDGE",EDGE,{"disambiguationData":[OSD([sQuery(id+"F20.wireOp",EDGE,"E98.top"),sQuery(id+"F20.wireOp",EDGE,"E98.right")])]})});
            var Q4;
            Q4=makeQuery(id+"F21.boolean.opBoolean","COPY",EDGE,{"derivedFrom":makeQuery(id+"F21.opExtrude","SWEPT_EDGE",EDGE,{"disambiguationData":[OSD([sQuery(id+"F20.wireOp",EDGE,"E98.top"),sQuery(id+"F20.wireOp",EDGE,"E98.left")])]})});
            var Q5;
            Q5=makeQuery(id+"F21.boolean.opBoolean","COPY",EDGE,{"derivedFrom":makeQuery(id+"F21.opExtrude","SWEPT_EDGE",EDGE,{"disambiguationData":[OSD([sQuery(id+"F20.wireOp",EDGE,"E98.bottom"),sQuery(id+"F20.wireOp",EDGE,"E98.right")])]})});
            fillet(context, id + "F22", {"entities" : qUnion([Q0, Q1, Q2, Q3, Q4, Q5]), "radius" : 2.54 * mm, "tangentPropagation" : true, "allowEdgeOverflow" : false});
        }
        {
            var Q0;
            Q0=makeQuery(id+"F1.opExtrude","SWEPT_BODY",BODY,{"disambiguationData":[OSD([sQuery(id+"F0.wireOp",EDGE,"E0.top"),sQuery(id+"F0.wireOp",EDGE,"E0.left"),sQuery(id+"F0.wireOp",EDGE,"E0.right"),sQuery(id+"F0.wireOp",EDGE,"E1"),sQuery(id+"F0.wireOp",EDGE,"E2"),sQuery(id+"F0.wireOp",EDGE,"E3"),sQuery(id+"F0.wireOp",EDGE,"E4"),sQuery(id+"F0.wireOp",EDGE,"E5"),sQuery(id+"F0.wireOp",EDGE,"E6"),sQuery(id+"F0.wireOp",EDGE,"E7")])]});
            var Q1;
            Q1=qCreatedBy(makeId("Right.planeOp"),FACE);
            mirror(context, id + "F23", {"operationType" : NewBodyOperationType.INTERSECT, "entities" : qUnion([Q0]), "mirrorPlane" : qUnion([Q1])});
        }
        {
            var Q0;
            {var subQ1=sQuery(id+"F9.wireOp",EDGE,"E83.bottom");Q0=makeQuery(id+"F9.imprint","IMPRINT",FACE,{"disambiguationData":[TD([[makeQuery(id+"F9.imprint","IMPRINT",EDGE,{"derivedFrom":subQ1}),1.0]])]});}
            extrude(context, id + "F24", {"entities" : qUnion([Q0]), "operationType" : NewBodyOperationType.REMOVE, "oppositeDirection" : true, "depth" : 25.4 * mm, "offsetDistance" : 25.4 * mm});
        }
        {
            var Q0;
            Q0=makeQuery(id+"F24.boolean.opBoolean","COPY",EDGE,{"derivedFrom":makeQuery(id+"F24.opExtrude","SWEPT_EDGE",EDGE,{"disambiguationData":[OSD([sQuery(id+"F9.wireOp",EDGE,"E83.top"),sQuery(id+"F9.wireOp",EDGE,"E83.left")])]})});
            fillet(context, id + "F25", {"entities" : qUnion([Q0]), "radius" : 5.08 * mm, "tangentPropagation" : true, "allowEdgeOverflow" : false});
        }
        {
            var Q0;
            Q0=makeQuery(id+"F1.opExtrude","CAP_EDGE",EDGE,{"disambiguationData":[OSD([sQuery(id+"F0.wireOp",EDGE,"E0.left")])],"isStart":true});
            var Q1;
            Q1=makeQuery(id+"F1.opExtrude","CAP_EDGE",EDGE,{"disambiguationData":[OSD([sQuery(id+"F0.wireOp",EDGE,"E0.right")])],"isStart":true});
            chamfer(context, id + "F26", {"entities" : qUnion([Q0, Q1]), "width" : 1.27 * mm, "tangentPropagation" : true});
        }
        {
            var Q0;
            Q0=makeQuery(id+"F1.opExtrude","CAP_EDGE",EDGE,{"disambiguationData":[OSD([sQuery(id+"F0.wireOp",EDGE,"E0.left")])],"isStart":false});
            var Q1;
            {var subQ0=sQuery(id+"F0.wireOp",EDGE,"E0.left");var subQ1=sQuery(id+"F0.wireOp",EDGE,"E0.top");Q1=makeQuery(id+"F24.boolean.opBoolean","SPLIT",EDGE,{"disambiguationData":[TD([makeQuery(id+"F7.boolean.opBoolean","COPY",FACE,{"derivedFrom":makeQuery(id+"F7.opExtrude","SWEPT_FACE",FACE,{"disambiguationData":[OSD([sQuery(id+"F6.wireOp",EDGE,"E71")])]})})])],"derivedFrom":makeQuery(id+"F1.opExtrude","SWEPT_EDGE",EDGE,{"disambiguationData":[OSD([subQ1,subQ0])]})});}
            var Q2;
            Q2=makeQuery(id+"F1.opExtrude","CAP_EDGE",EDGE,{"disambiguationData":[OSD([sQuery(id+"F0.wireOp",EDGE,"E0.top")])],"isStart":false});
            var Q3;
            Q3=makeQuery(id+"F1.opExtrude","CAP_EDGE",EDGE,{"disambiguationData":[OSD([sQuery(id+"F0.wireOp",EDGE,"E0.right")])],"isStart":false});
            var Q4;
            Q4=makeQuery(id+"F1.opExtrude","SWEPT_EDGE",EDGE,{"disambiguationData":[OSD([sQuery(id+"F0.wireOp",EDGE,"E0.top"),sQuery(id+"F0.wireOp",EDGE,"E0.right")])]});
            var Q5;
            {var subQ0=sQuery(id+"F6.wireOp",EDGE,"E61");var subQ1=sQuery(id+"F0.wireOp",EDGE,"E0.left");var subQ2=sQuery(id+"F0.wireOp",EDGE,"E0.top");Q5=makeQuery(id+"F24.boolean.opBoolean","SPLIT",EDGE,{"disambiguationData":[TD([makeQuery(id+"F7.boolean.opBoolean","COPY",FACE,{"derivedFrom":makeQuery(id+"F7.opExtrude","SWEPT_FACE",FACE,{"disambiguationData":[OSD([subQ0])]})})])],"derivedFrom":makeQuery(id+"F1.opExtrude","SWEPT_EDGE",EDGE,{"disambiguationData":[OSD([subQ2,subQ1])]})});}
            fillet(context, id + "F27", {"entities" : qUnion([Q0, Q1, Q2, Q3, Q4, Q5]), "radius" : 5.08 * mm, "tangentPropagation" : true, "allowEdgeOverflow" : false});
        }
    });
